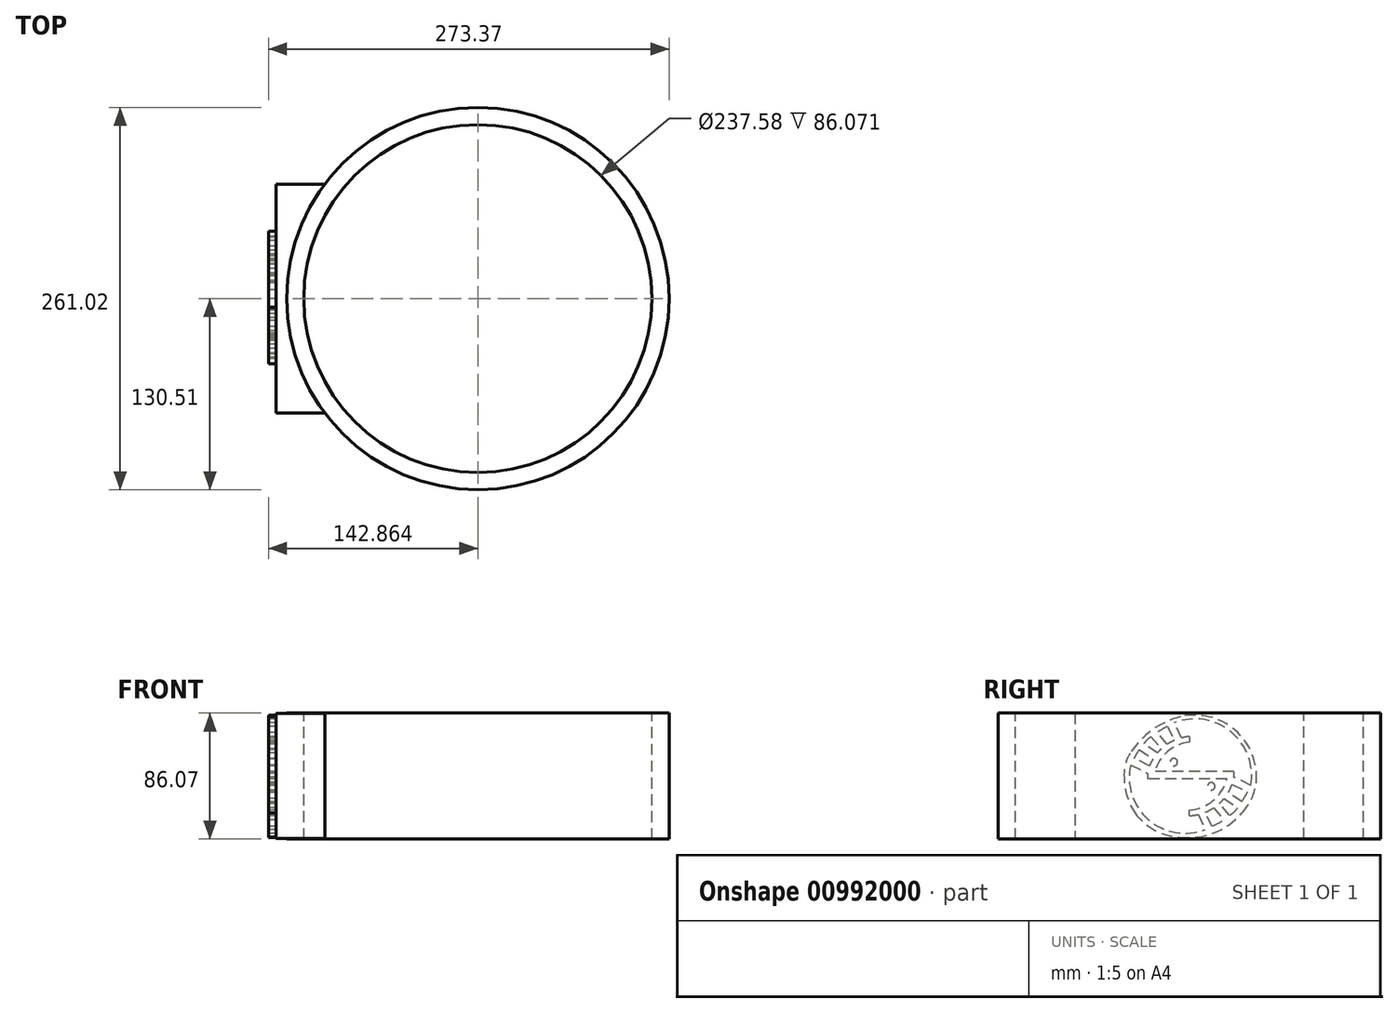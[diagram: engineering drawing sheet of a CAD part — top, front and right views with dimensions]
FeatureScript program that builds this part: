
annotation { "Feature Type Name" : "Feature", "Feature Type Description" : "" }
export const myFeature = defineFeature(function(context is Context, id is Id, definition is map)
    precondition{}
    {
        {
            var Q0;
            Q0=qCreatedBy(makeId("Front.planeOp"),FACE);
            var sketch = newSketch(context, id + "F0", { "sketchPlane" : qUnion([Q0])});
            skLineSegment(sketch, "E0.bottom", {"start": v(-28.6, 62.64) * mm, "end": v(-16.88, 62.64) * mm});
            skLineSegment(sketch, "E0.top", {"start": v(-28.6, -23.43) * mm, "end": v(-16.88, -23.43) * mm});
            skLineSegment(sketch, "E0.left", {"start": v(-28.6, 62.64) * mm, "end": v(-28.6, -23.43) * mm});
            skLineSegment(sketch, "E0.right", {"start": v(-16.88, 62.64) * mm, "end": v(-16.88, -23.43) * mm});
            skLineSegment(sketch, "E1", {"start": v(101.91, 62.64) * mm, "end": v(101.91, -23.43) * mm});
            skSolve(sketch);
        }
        {
            var Q0;
            Q0=makeQuery(id+"F0.imprint","IMPRINT",FACE,{"disambiguationData":[TD([[makeQuery(id+"F0.imprint","IMPRINT",EDGE,{"derivedFrom":sQuery(id+"F0.wireOp",EDGE,"E0.bottom")}),-1.0]])]});
            var Q1;
            Q1=sQuery(id+"F0.wireOp",EDGE,"E1");
            revolve(context, id + "F1", {"surfaceOperationType" : NewSurfaceOperationType.NEW, "entities" : qUnion([Q0]), "axis" : qUnion([Q1]), "revolveType" : RevolveType.FULL});
        }
        {
            var Q0;
            Q0=qCreatedBy(makeId("Top.planeOp"),FACE);
            var sketch = newSketch(context, id + "F2", { "sketchPlane" : qUnion([Q0])});
            skLineSegment(sketch, "E2", {"start": v(0, 78.18) * mm, "end": v(-23.88, 0) * mm});
            skLineSegment(sketch, "E3", {"start": v(-23.88, 0) * mm, "end": v(0, -78.18) * mm});
            skLineSegment(sketch, "E4", {"start": v(0, -78.18) * mm, "end": v(-40.95, -78.18) * mm});
            skLineSegment(sketch, "E5", {"start": v(-40.95, -78.18) * mm, "end": v(-40.95, 78.18) * mm});
            skLineSegment(sketch, "E6", {"start": v(-40.95, 78.18) * mm, "end": v(0, 78.18) * mm});
            skSolve(sketch);
        }
        {
            var Q0;
            Q0=makeQuery(id+"F2.imprint","IMPRINT",FACE,{"disambiguationData":[TD([[makeQuery(id+"F2.imprint","IMPRINT",EDGE,{"derivedFrom":sQuery(id+"F2.wireOp",EDGE,"3QXirezC-aCE7-lBuO-2HS4-it67jw9ABbBA.bottom")}),-1.0]])]});
            var Q1;
            Q1=makeQuery(id+"F2.imprint","IMPRINT",FACE,{"disambiguationData":[TD([[makeQuery(id+"F2.imprint","IMPRINT",EDGE,{"derivedFrom":sQuery(id+"F2.wireOp",EDGE,"E2")}),-1.0]])]});
            extrude(context, id + "F3", {"entities" : qUnion([Q0, Q1]), "operationType" : NewBodyOperationType.ADD, "depth" : 62.48 * mm, "offsetDistance" : 25.4 * mm, "hasSecondDirection" : true, "secondDirectionOppositeDirection" : true, "secondDirectionDepth" : 23.1 * mm});
        }
        {
            var Q0;
            Q0=makeQuery(id+"F3.opExtrude","SWEPT_FACE",FACE,{"disambiguationData":[OSD([sQuery(id+"F2.wireOp",EDGE,"E5")])]});
            var sketch = newSketch(context, id + "F4", { "sketchPlane" : qUnion([Q0])});
            skLineSegment(sketch, "E7.bottom", {"start": v(-30.27, 22.67) * mm, "end": v(28.52, 22.67) * mm});
            skLineSegment(sketch, "E7.top", {"start": v(-30.27, 17.75) * mm, "end": v(28.52, 17.75) * mm});
            skLineSegment(sketch, "E7.left", {"start": v(-30.27, 22.67) * mm, "end": v(-30.27, 17.75) * mm});
            skLineSegment(sketch, "E7.right", {"start": v(28.52, 22.67) * mm, "end": v(28.52, 17.75) * mm});
            skArc(sketch, "E8", {"start": v(28.52, 22.67) * mm, "mid": v(18.03, 39.12) * mm, "end": v(0, 46.57) * mm});
            skArc(sketch, "E9", {"start": v(-30.27, 17.75) * mm, "mid": v(-19.42, 0) * mm, "end": v(0, -7.47) * mm});
            skLineSegment(sketch, "E10", {"start": v(0, 46.57) * mm, "end": v(0, 42.72) * mm});
            skLineSegment(sketch, "E11", {"start": v(0, -7.47) * mm, "end": v(0, -3.63) * mm});
            skArc(sketch, "E12", {"start": v(23.7, 22.67) * mm, "mid": v(14.86, 36.25) * mm, "end": v(0, 42.72) * mm});
            skArc(sketch, "E13", {"start": v(-25.6, 17.75) * mm, "mid": v(-16.3, 2.87) * mm, "end": v(0, -3.63) * mm});
            skCircle(sketch, "E14", {"center": v(10.58, 29.08) * mm, "radius": 2.52 * mm});
            skCircle(sketch, "E15", {"center": v(-14.95, 12.64) * mm, "radius": 2.52 * mm});
            skLineSegment(sketch, "E16", {"start": v(-6, -6.66) * mm, "end": v(-10.93, -16.92) * mm});
            skLineSegment(sketch, "E17", {"start": v(-10.93, -16.92) * mm, "end": v(-15.5, -14.72) * mm});
            skLineSegment(sketch, "E18", {"start": v(-15.5, -14.72) * mm, "end": v(-10.89, -5.12) * mm});
            skLineSegment(sketch, "E19", {"start": v(-16.44, -2.2) * mm, "end": v(-23.55, -10.47) * mm});
            skLineSegment(sketch, "E20", {"start": v(-23.55, -10.47) * mm, "end": v(-27.4, -7.17) * mm});
            skLineSegment(sketch, "E21", {"start": v(-27.4, -7.17) * mm, "end": v(-20.45, 0.9) * mm});
            skLineSegment(sketch, "E22", {"start": v(-23.61, 4.2) * mm, "end": v(-32.97, -2.05) * mm});
            skLineSegment(sketch, "E23", {"start": v(-32.97, -2.05) * mm, "end": v(-35.79, 2.16) * mm});
            skLineSegment(sketch, "E24", {"start": v(-35.79, 2.16) * mm, "end": v(-26.53, 8.35) * mm});
            skLineSegment(sketch, "E25", {"start": v(-29.13, 13.83) * mm, "end": v(-39.61, 8.63) * mm});
            skLineSegment(sketch, "E26", {"start": v(-39.61, 8.63) * mm, "end": v(-41.87, 13.17) * mm});
            skLineSegment(sketch, "E27", {"start": v(-41.87, 13.17) * mm, "end": v(-30.27, 18.93) * mm});
            skLineSegment(sketch, "E28.1.0", {"start": v(40.11, 27.2) * mm, "end": v(28.52, 21.44) * mm});
            skLineSegment(sketch, "E28.1.1", {"start": v(37.7, 31.74) * mm, "end": v(40.11, 27.2) * mm});
            skLineSegment(sketch, "E28.1.2", {"start": v(27.22, 26.54) * mm, "end": v(37.7, 31.74) * mm});
            skLineSegment(sketch, "E28.1.3", {"start": v(34.16, 37.55) * mm, "end": v(24.8, 31.3) * mm});
            skLineSegment(sketch, "E28.1.4", {"start": v(21.8, 35.4) * mm, "end": v(31.06, 41.58) * mm});
            skLineSegment(sketch, "E28.1.5", {"start": v(31.06, 41.58) * mm, "end": v(34.16, 37.55) * mm});
            skLineSegment(sketch, "E28.1.6", {"start": v(26.21, 46.46) * mm, "end": v(19.1, 38.2) * mm});
            skLineSegment(sketch, "E28.1.7", {"start": v(22.04, 49.39) * mm, "end": v(26.21, 46.46) * mm});
            skLineSegment(sketch, "E28.1.8", {"start": v(15.1, 41.31) * mm, "end": v(22.04, 49.39) * mm});
            skLineSegment(sketch, "E28.1.9", {"start": v(14.87, 53.56) * mm, "end": v(10.26, 43.95) * mm});
            skLineSegment(sketch, "E28.1.10", {"start": v(10.36, 55.88) * mm, "end": v(14.87, 53.56) * mm});
            skLineSegment(sketch, "E28.1.11", {"start": v(5.43, 45.63) * mm, "end": v(10.36, 55.88) * mm});
            skArc(sketch, "E29", {"start": v(22.04, 49.39) * mm, "mid": v(18.5, 51.56) * mm, "end": v(14.87, 53.56) * mm});
            skArc(sketch, "E30", {"start": v(31.06, 41.58) * mm, "mid": v(28.8, 44.18) * mm, "end": v(26.21, 46.46) * mm});
            skArc(sketch, "E31", {"start": v(37.7, 31.74) * mm, "mid": v(36.09, 34.74) * mm, "end": v(34.16, 37.55) * mm});
            skArc(sketch, "E32", {"start": v(-10.93, -16.92) * mm, "mid": v(27.85, -10.2) * mm, "end": v(40.11, 27.2) * mm});
            skArc(sketch, "E33", {"start": v(-23.55, -10.47) * mm, "mid": v(-19.57, -12.67) * mm, "end": v(-15.5, -14.72) * mm});
            skArc(sketch, "E34", {"start": v(-32.97, -2.05) * mm, "mid": v(-30.49, -4.94) * mm, "end": v(-27.4, -7.17) * mm});
            skArc(sketch, "E35", {"start": v(-39.61, 8.63) * mm, "mid": v(-37.82, 5.32) * mm, "end": v(-35.79, 2.16) * mm});
            skArc(sketch, "E36", {"start": v(10.36, 55.88) * mm, "mid": v(-28.3, 49.86) * mm, "end": v(-41.87, 13.17) * mm});
            skArc(sketch, "E37", {"start": v(6.14, 60.1) * mm, "mid": v(-31.15, 50.98) * mm, "end": v(-45.8, 15.5) * mm});
            skArc(sketch, "E38", {"start": v(-45.8, 15.5) * mm, "mid": v(-42.47, 4.14) * mm, "end": v(-35.83, -5.66) * mm});
            skArc(sketch, "E39", {"start": v(43.57, 29.44) * mm, "mid": v(28.2, 48.85) * mm, "end": v(6.14, 60.1) * mm});
            skArc(sketch, "E40", {"start": v(37.1, -5.7) * mm, "mid": v(43.81, 11.23) * mm, "end": v(43.57, 29.44) * mm});
            skArc(sketch, "E41", {"start": v(7.16, -22.1) * mm, "mid": v(23.92, -17.18) * mm, "end": v(37.1, -5.7) * mm});
            skArc(sketch, "E42", {"start": v(-35.83, -5.66) * mm, "mid": v(-16.4, -19.3) * mm, "end": v(7.16, -22.1) * mm});
            skSolve(sketch);
        }
        {
            var Q0;
            {var subQ0=sQuery(id+"F4.wireOp",EDGE,"E10");Q0=makeQuery(id+"F4.imprint","IMPRINT",FACE,{"disambiguationData":[TD([[makeQuery(id+"F4.imprint","IMPRINT",EDGE,{"derivedFrom":subQ0}),-1.0]])]});}
            var Q1;
            {var subQ0=sQuery(id+"F4.wireOp",EDGE,"E11");Q1=makeQuery(id+"F4.imprint","IMPRINT",FACE,{"disambiguationData":[TD([[makeQuery(id+"F4.imprint","IMPRINT",EDGE,{"derivedFrom":subQ0}),-1.0]])]});}
            var Q2;
            {var subQ0=sQuery(id+"F4.wireOp",EDGE,"E28.1.2");Q2=makeQuery(id+"F4.imprint","IMPRINT",FACE,{"disambiguationData":[TD([[makeQuery(id+"F4.imprint","IMPRINT",EDGE,{"derivedFrom":subQ0}),1.0]])]});}
            var Q3;
            {var subQ0=sQuery(id+"F4.wireOp",EDGE,"E28.1.4");Q3=makeQuery(id+"F4.imprint","IMPRINT",FACE,{"disambiguationData":[TD([[makeQuery(id+"F4.imprint","IMPRINT",EDGE,{"derivedFrom":subQ0}),1.0]])]});}
            var Q4;
            {var subQ0=sQuery(id+"F4.wireOp",EDGE,"E28.1.8");Q4=makeQuery(id+"F4.imprint","IMPRINT",FACE,{"disambiguationData":[TD([[makeQuery(id+"F4.imprint","IMPRINT",EDGE,{"derivedFrom":subQ0}),1.0]])]});}
            var Q5;
            {var subQ0=sQuery(id+"F4.wireOp",EDGE,"E18");Q5=makeQuery(id+"F4.imprint","IMPRINT",FACE,{"disambiguationData":[TD([[makeQuery(id+"F4.imprint","IMPRINT",EDGE,{"derivedFrom":subQ0}),1.0]])]});}
            var Q6;
            {var subQ0=sQuery(id+"F4.wireOp",EDGE,"E21");Q6=makeQuery(id+"F4.imprint","IMPRINT",FACE,{"disambiguationData":[TD([[makeQuery(id+"F4.imprint","IMPRINT",EDGE,{"derivedFrom":subQ0}),1.0]])]});}
            var Q7;
            {var subQ0=sQuery(id+"F4.wireOp",EDGE,"E24");Q7=makeQuery(id+"F4.imprint","IMPRINT",FACE,{"disambiguationData":[TD([[makeQuery(id+"F4.imprint","IMPRINT",EDGE,{"derivedFrom":subQ0}),1.0]])]});}
            var Q8;
            Q8=makeQuery(id+"F4.imprint","IMPRINT",FACE,{"disambiguationData":[TD([[makeQuery(id+"F4.imprint","IMPRINT",EDGE,{"derivedFrom":sQuery(id+"F4.wireOp",EDGE,"E37")}),-1.0]])]});
            extrude(context, id + "F5", {"entities" : qUnion([Q0, Q1, Q2, Q3, Q4, Q5, Q6, Q7, Q8]), "operationType" : NewBodyOperationType.REMOVE, "oppositeDirection" : true, "depth" : 5.08 * mm, "offsetDistance" : 25.4 * mm});
        }
        {
            var Q0;
            Q0=makeQuery(id+"F5.boolean.opBoolean","COPY",EDGE,{"derivedFrom":makeQuery(id+"F5.opExtrude","SWEPT_EDGE",EDGE,{"disambiguationData":[OSD([sQuery(id+"F4.wireOp",EDGE,"E39"),sQuery(id+"F4.wireOp",EDGE,"E40")])]})});
            fillet(context, id + "F6", {"entities" : qUnion([Q0]), "radius" : 26.6 * mm, "tangentPropagation" : true, "allowEdgeOverflow" : false});
        }
    });
